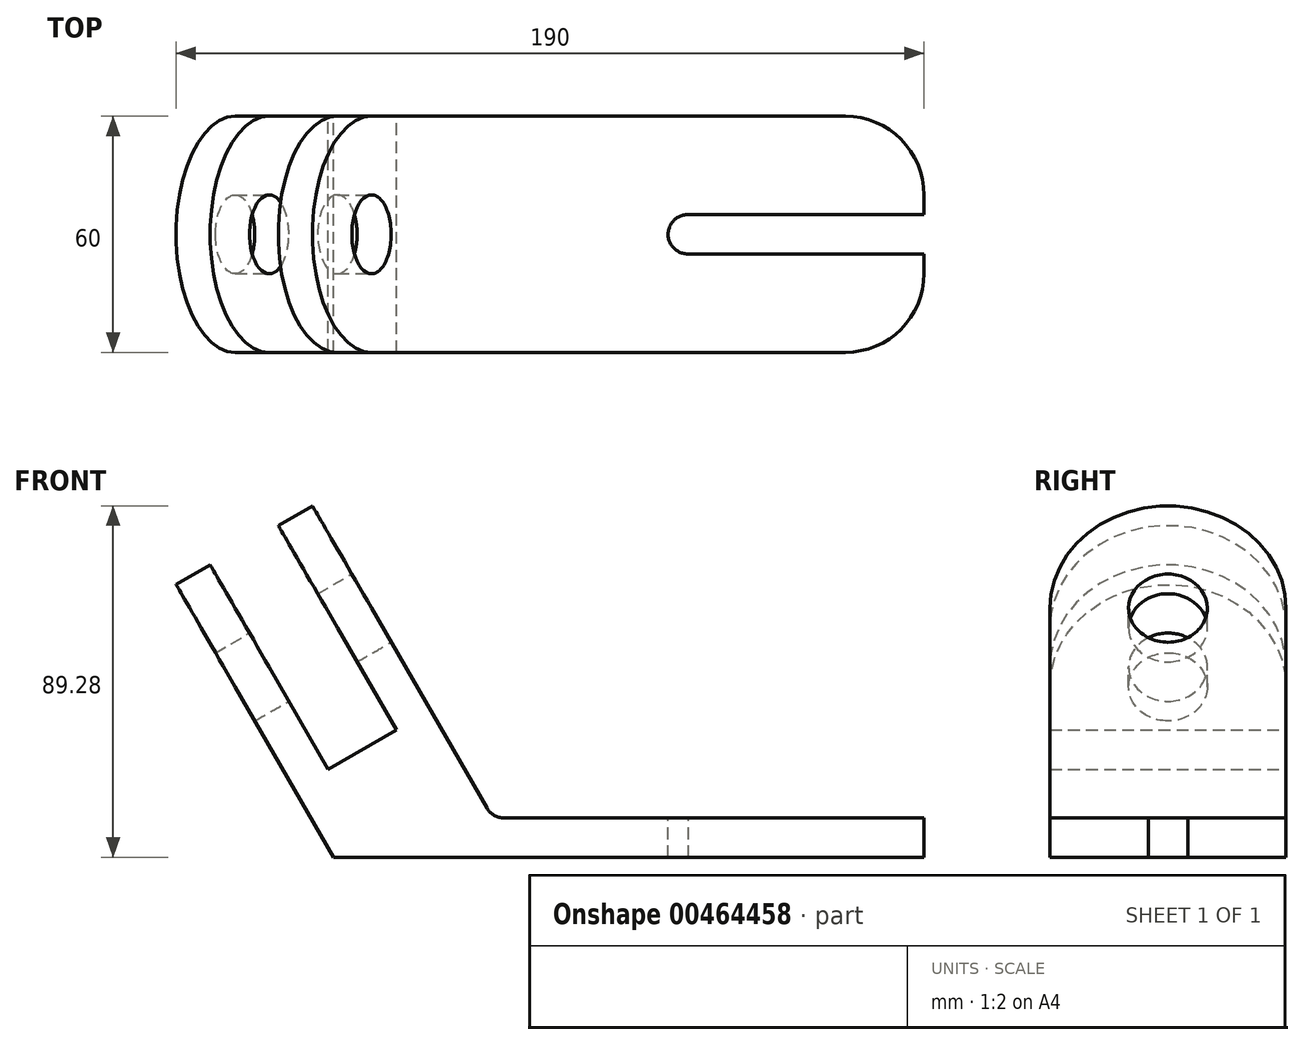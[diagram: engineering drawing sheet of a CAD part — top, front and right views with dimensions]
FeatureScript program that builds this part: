
annotation { "Feature Type Name" : "Feature", "Feature Type Description" : "" }
export const myFeature = defineFeature(function(context is Context, id is Id, definition is map)
    precondition{}
    {
        {
            var Q0;
            Q0=qCreatedBy(makeId("Front.planeOp"),FACE);
            var sketch = newSketch(context, id + "F0", { "sketchPlane" : qUnion([Q0])});
            skLineSegment(sketch, "E0", {"start": v(0, 0) * mm, "end": v(150, 0) * mm});
            skLineSegment(sketch, "E1", {"start": v(150, 0) * mm, "end": v(150, 10) * mm});
            skLineSegment(sketch, "E2", {"start": v(0, 0) * mm, "end": v(-40, 69.28) * mm});
            skLineSegment(sketch, "E3", {"start": v(-5.36, 89.28) * mm, "end": v(38.97, 12.5) * mm});
            skLineSegment(sketch, "E4", {"start": v(43.3, 10) * mm, "end": v(150, 10) * mm});
            skLineSegment(sketch, "E5", {"start": v(-31.34, 74.28) * mm, "end": v(-1.34, 22.32) * mm});
            skLineSegment(sketch, "E6", {"start": v(-14.02, 84.28) * mm, "end": v(15.98, 32.32) * mm});
            skLineSegment(sketch, "E7", {"start": v(-1.34, 22.32) * mm, "end": v(15.98, 32.32) * mm});
            skLineSegment(sketch, "E8", {"start": v(-40, 69.28) * mm, "end": v(-31.34, 74.28) * mm});
            skLineSegment(sketch, "E9", {"start": v(-14.02, 84.28) * mm, "end": v(-5.36, 89.28) * mm});
            skPoint(sketch, "E10.visualSharp", {"position": v(40.41, 10) * mm});
            skArc(sketch, "E10.filletArc", {"start": v(38.97, 12.5) * mm, "mid": v(40.8, 10.67) * mm, "end": v(43.3, 10) * mm});
            skSolve(sketch);
        }
        {
            var Q0;
            Q0 = qSketchRegion(id + "F0", true);
            extrude(context, id + "F1", {"entities" : qUnion([Q0]), "depth" : 60 * mm, "offsetDistance" : 25 * mm});
        }
        {
            var Q0;
            Q0=makeQuery(id+"F1.opExtrude","CAP_EDGE",EDGE,{"disambiguationData":[OSD([sQuery(id+"F0.wireOp",EDGE,"E1")])],"isStart":true});
            var Q1;
            Q1=makeQuery(id+"F1.opExtrude","CAP_EDGE",EDGE,{"disambiguationData":[OSD([sQuery(id+"F0.wireOp",EDGE,"E1")])],"isStart":false});
            fillet(context, id + "F2", {"entities" : qUnion([Q0, Q1]), "radius" : 20 * mm, "tangentPropagation" : true, "allowEdgeOverflow" : false});
        }
        {
            var Q0;
            Q0=makeQuery(id+"F1.opExtrude","SWEPT_FACE",FACE,{"disambiguationData":[OSD([sQuery(id+"F0.wireOp",EDGE,"E4")])]});
            var sketch = newSketch(context, id + "F3", { "sketchPlane" : qUnion([Q0])});
            skCircle(sketch, "E11", {"center": v(90, -30) * mm, "radius": 5 * mm});
            skPoint(sketch, "E11.centerSnap0", {"position": v(150, -30) * mm});
            skLineSegment(sketch, "E12", {"start": v(90.13, -25) * mm, "end": v(150, -25) * mm});
            skLineSegment(sketch, "E13", {"start": v(90, -35) * mm, "end": v(150, -35) * mm});
            skSolve(sketch);
        }
        {
            var Q0;
            Q0 = qSketchRegion(id + "F3", true);
            var Q1;
            {var subQ0=sQuery(id+"F3.wireOp",EDGE,"E12");Q1=makeQuery(id+"F3.imprint","IMPRINT",FACE,{"disambiguationData":[TD([[makeQuery(id+"F3.imprint","IMPRINT",EDGE,{"derivedFrom":subQ0}),-1.0]])]});}
            extrude(context, id + "F4", {"entities" : qUnion([Q0, Q1]), "operationType" : NewBodyOperationType.REMOVE, "endBound" : BoundingType.THROUGH_ALL, "oppositeDirection" : true, "depth" : 25 * mm, "offsetDistance" : 25 * mm});
        }
        {
            var Q0;
            Q0=makeQuery(id+"F1.opExtrude","CAP_EDGE",EDGE,{"disambiguationData":[OSD([sQuery(id+"F0.wireOp",EDGE,"E9")])],"isStart":false});
            var Q1;
            Q1=makeQuery(id+"F1.opExtrude","CAP_EDGE",EDGE,{"disambiguationData":[OSD([sQuery(id+"F0.wireOp",EDGE,"E9")])],"isStart":true});
            var Q2;
            Q2=makeQuery(id+"F1.opExtrude","CAP_EDGE",EDGE,{"disambiguationData":[OSD([sQuery(id+"F0.wireOp",EDGE,"E8")])],"isStart":false});
            var Q3;
            Q3=makeQuery(id+"F1.opExtrude","CAP_EDGE",EDGE,{"disambiguationData":[OSD([sQuery(id+"F0.wireOp",EDGE,"E8")])],"isStart":true});
            fillet(context, id + "F5", {"entities" : qUnion([Q0, Q1, Q2, Q3]), "radius" : 30 * mm, "tangentPropagation" : true, "allowEdgeOverflow" : false});
        }
        {
            var Q0;
            Q0=makeQuery(id+"F1.opExtrude","SWEPT_FACE",FACE,{"disambiguationData":[OSD([sQuery(id+"F0.wireOp",EDGE,"E3")])]});
            var sketch = newSketch(context, id + "F6", { "sketchPlane" : qUnion([Q0])});
            skPoint(sketch, "E14.centerSnap0", {"position": v(-30, 80) * mm});
            skCircle(sketch, "E15", {"center": v(-30, 50) * mm, "radius": 10 * mm});
            skSolve(sketch);
        }
        {
            var Q0;
            Q0=sQuery(id+"F6.wireOp",VERTEX,"E15.center");
            var Q1;
            Q1=makeQuery(id+"F1.opExtrude","SWEPT_BODY",BODY,{"disambiguationData":[OSD([sQuery(id+"F0.wireOp",EDGE,"E0"),sQuery(id+"F0.wireOp",EDGE,"E1"),sQuery(id+"F0.wireOp",EDGE,"E2"),sQuery(id+"F0.wireOp",EDGE,"E3"),sQuery(id+"F0.wireOp",EDGE,"E4"),sQuery(id+"F0.wireOp",EDGE,"E5"),sQuery(id+"F0.wireOp",EDGE,"E6"),sQuery(id+"F0.wireOp",EDGE,"E7"),sQuery(id+"F0.wireOp",EDGE,"E8"),sQuery(id+"F0.wireOp",EDGE,"E9"),sQuery(id+"F0.wireOp",EDGE,"E10.filletArc")])]});
            hole(context, id + "F7", {"style" : HoleStyle.SIMPLE, "endStyle" : HoleEndStyle.THROUGH, "holeDiameter" : 20 * mm, "majorDiameter" : 5 * mm, "isTappedThrough" : true, "tappedDepth" : 12 * mm, "tapClearance" : 3, "locations" : qUnion([Q0]), "scope" : qUnion([Q1])});
        }
    });
